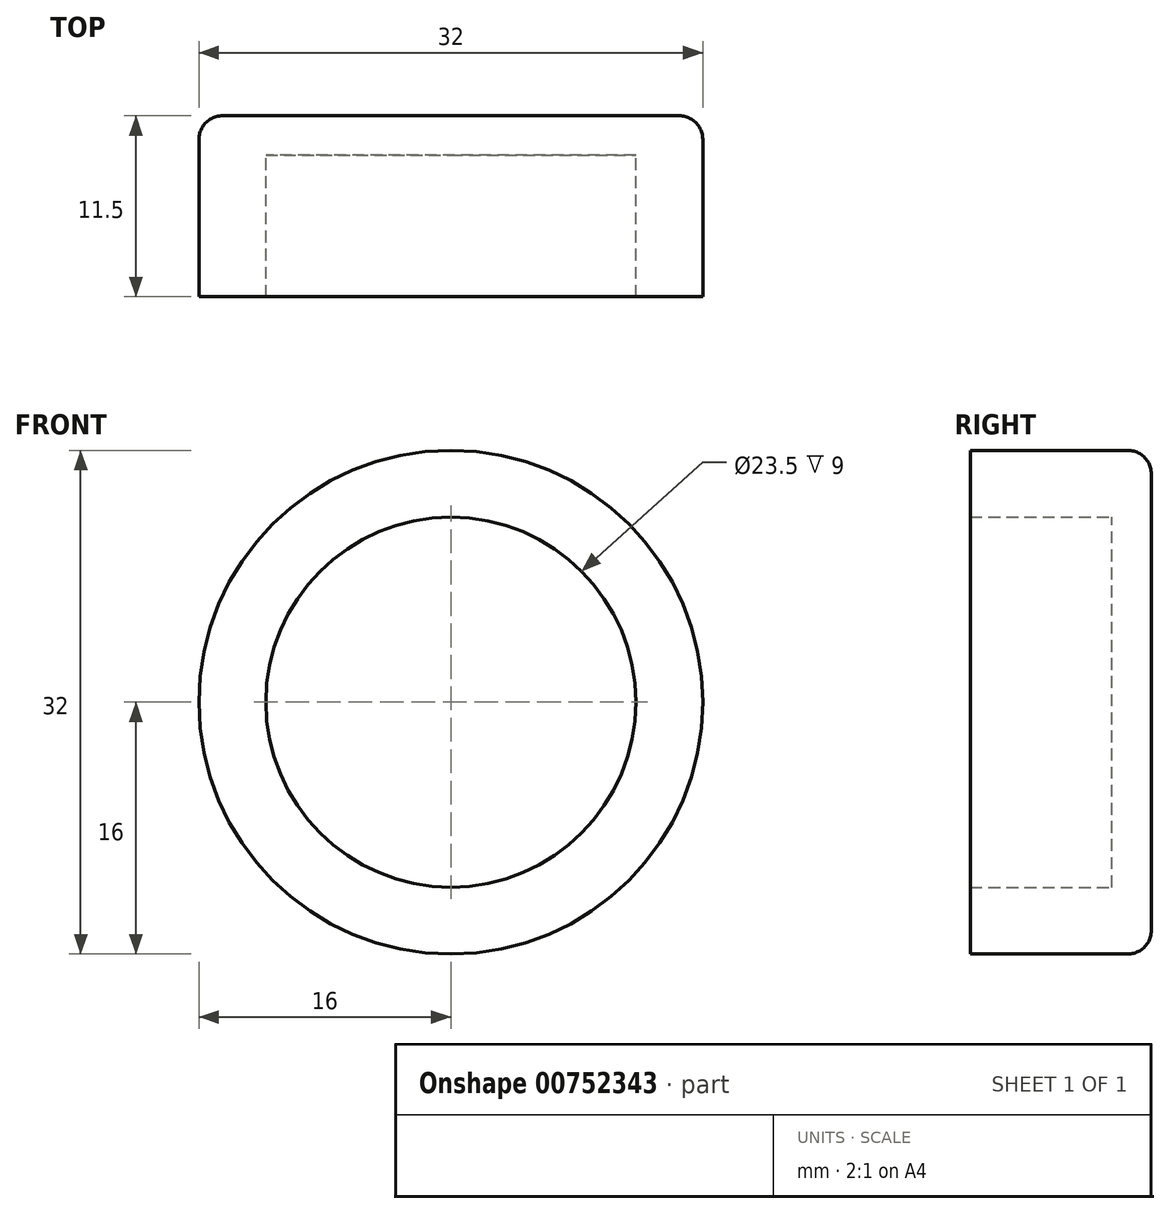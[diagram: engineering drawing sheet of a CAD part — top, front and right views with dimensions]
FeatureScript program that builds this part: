
annotation { "Feature Type Name" : "Feature", "Feature Type Description" : "" }
export const myFeature = defineFeature(function(context is Context, id is Id, definition is map)
    precondition{}
    {
        {
            var Q0;
            Q0=qCreatedBy(makeId("Front.planeOp"),FACE);
            var sketch = newSketch(context, id + "F0", { "sketchPlane" : qUnion([Q0])});
            skCircle(sketch, "E0", {"center": v(0, 0) * mm, "radius": 16 * mm});
            skSolve(sketch);
        }
        {
            var Q0;
            Q0=qSketchRegion(id+"F0",true);
            extrude(context, id + "F1", {"entities" : qUnion([Q0]), "depth" : 2.5 * mm, "offsetDistance" : 25 * mm});
        }
        {
            var Q0;
            Q0=makeQuery(id+"F1.opExtrude","CAP_FACE",FACE,{"disambiguationData":[OSD([sQuery(id+"F0.wireOp",EDGE,"E0")])],"isStart":false});
            var sketch = newSketch(context, id + "F2", { "sketchPlane" : qUnion([Q0])});
            skCircle(sketch, "E1", {"center": v(0, 0) * mm, "radius": 11.75 * mm});
            skCircle(sketch, "E2", {"center": v(0, 0) * mm, "radius": 16 * mm});
            skSolve(sketch);
        }
        {
            var Q0;
            Q0=qSketchRegion(id+"F2",true);
            extrude(context, id + "F3", {"entities" : qUnion([Q0]), "operationType" : NewBodyOperationType.ADD, "depth" : 9 * mm, "offsetDistance" : 25 * mm});
        }
        {
            var Q0;
            Q0=makeQuery(id+"F1.opExtrude","CAP_FACE",FACE,{"disambiguationData":[OSD([sQuery(id+"F0.wireOp",EDGE,"E0")])],"isStart":true});
            fillet(context, id + "F4", {"entities" : qUnion([Q0]), "radius" : 1.5 * mm, "tangentPropagation" : true, "allowEdgeOverflow" : false});
        }
    });
